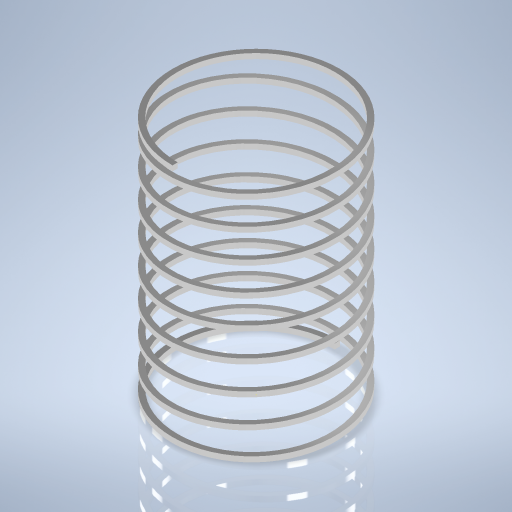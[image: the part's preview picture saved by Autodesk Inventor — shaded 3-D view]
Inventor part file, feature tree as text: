
AUTODESK INVENTOR PART (.ipt)
format: ipt  version: 2024 (Build 280153000, 153)  size: 685,056 bytes
history: native  units: mm
features: sketch x2, other x1
ambient origin geometry x8: Origin, YZ Plane, XZ Plane, XY Plane, X Axis, Y Axis, Z Axis, Center Point
bodies: Volumenkörper1 (feature_tree)
feature tree (3):
  other  "Spirale1"
  sketch  "Skizze3"  dims[d1=4.0mm d2=4.0mm d3=120.0mm d4=20.0mm d5=180.0mm d6=80.0mm d7=0.0mm d8=90.0deg d9=180.0deg d10=90.0deg d11=180.0deg]
  sketch  "Skizze1"  dims[d0=180.0mm]
